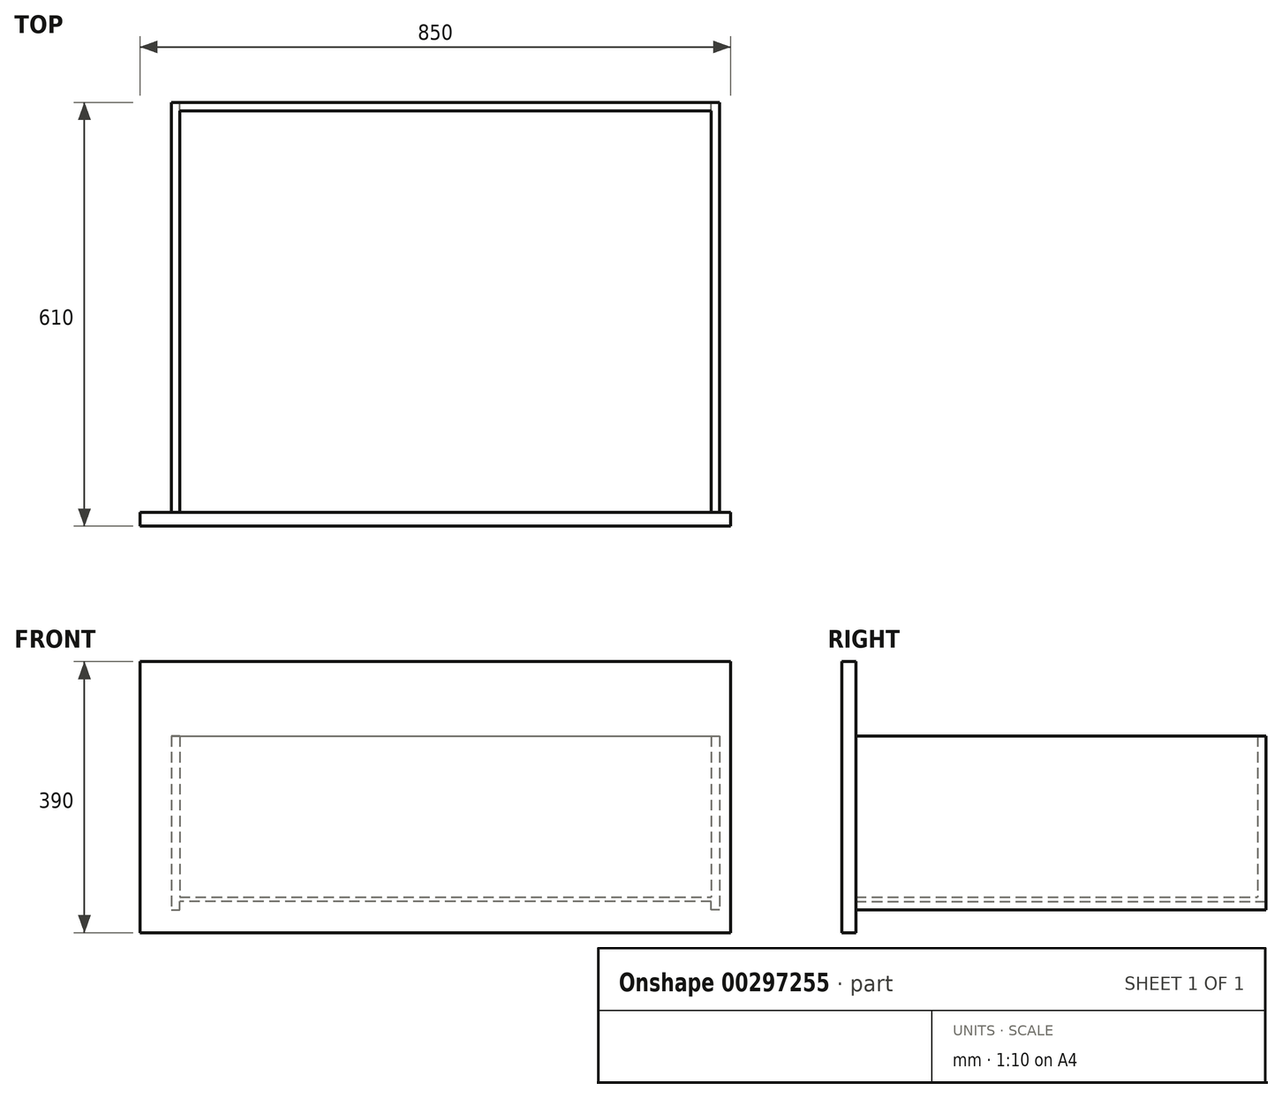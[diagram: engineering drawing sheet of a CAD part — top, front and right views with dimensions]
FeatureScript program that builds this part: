
annotation { "Feature Type Name" : "Feature", "Feature Type Description" : "" }
export const myFeature = defineFeature(function(context is Context, id is Id, definition is map)
    precondition{}
    {
        {
            var Q0;
            Q0=qCreatedBy(makeId("Front.planeOp"),FACE);
            var sketch = newSketch(context, id + "F0", { "sketchPlane" : qUnion([Q0])});
            skLineSegment(sketch, "E0.bottom", {"start": v(382.49, -3) * mm, "end": v(-382.51, -3) * mm});
            skLineSegment(sketch, "E0.top", {"start": v(382.51, 3) * mm, "end": v(-382.49, 3) * mm});
            skPoint(sketch, "E0.middle", {"position": v(0, 0) * mm});
            skLineSegment(sketch, "E1", {"start": v(-382.49, 3) * mm, "end": v(-382.49, 235) * mm});
            skLineSegment(sketch, "E2", {"start": v(-382.49, 235) * mm, "end": v(-394.49, 235) * mm});
            skLineSegment(sketch, "E3", {"start": v(-394.49, 235) * mm, "end": v(-394.49, -15) * mm});
            skLineSegment(sketch, "E4", {"start": v(-394.49, -15) * mm, "end": v(-382.49, -15) * mm});
            skLineSegment(sketch, "E5", {"start": v(-382.49, -15) * mm, "end": v(-382.51, -3) * mm});
            skLineSegment(sketch, "E6", {"start": v(382.51, 3) * mm, "end": v(382.51, 235) * mm});
            skLineSegment(sketch, "E7", {"start": v(382.51, 235) * mm, "end": v(394.51, 235) * mm});
            skLineSegment(sketch, "E8", {"start": v(394.51, 235) * mm, "end": v(394.51, -15) * mm});
            skLineSegment(sketch, "E9", {"start": v(394.51, -15) * mm, "end": v(382.51, -15) * mm});
            skLineSegment(sketch, "E10", {"start": v(382.51, -15) * mm, "end": v(382.49, -3) * mm});
            skSolve(sketch);
        }
        {
            var Q0;
            Q0=qSketchRegion(id+"F0",true);
            extrude(context, id + "F1", {"entities" : qUnion([Q0]), "depth" : 590 * mm});
        }
        {
            var Q0;
            Q0=makeQuery(id+"F1.opExtrude","CAP_FACE",FACE,{"disambiguationData":[OSD([sQuery(id+"F0.wireOp",EDGE,"E0.bottom"),sQuery(id+"F0.wireOp",EDGE,"E0.top"),sQuery(id+"F0.wireOp",EDGE,"E1"),sQuery(id+"F0.wireOp",EDGE,"E2"),sQuery(id+"F0.wireOp",EDGE,"E3"),sQuery(id+"F0.wireOp",EDGE,"E4"),sQuery(id+"F0.wireOp",EDGE,"E5"),sQuery(id+"F0.wireOp",EDGE,"E6"),sQuery(id+"F0.wireOp",EDGE,"E7"),sQuery(id+"F0.wireOp",EDGE,"E8"),sQuery(id+"F0.wireOp",EDGE,"E9"),sQuery(id+"F0.wireOp",EDGE,"E10")])],"isStart":false});
            var sketch = newSketch(context, id + "F2", { "sketchPlane" : qUnion([Q0])});
            skLineSegment(sketch, "E11.bottom", {"start": v(-439.49, 342) * mm, "end": v(410.51, 342) * mm});
            skLineSegment(sketch, "E11.top", {"start": v(-439.49, -48) * mm, "end": v(410.51, -48) * mm});
            skLineSegment(sketch, "E11.left", {"start": v(-439.49, 342) * mm, "end": v(-439.49, -48) * mm});
            skLineSegment(sketch, "E11.right", {"start": v(410.51, 342) * mm, "end": v(410.51, -48) * mm});
            skSolve(sketch);
        }
        {
            var Q0;
            Q0=qSketchRegion(id+"F2",true);
            extrude(context, id + "F3", {"entities" : qUnion([Q0]), "operationType" : NewBodyOperationType.ADD, "depth" : 20 * mm});
        }
        {
            var Q0;
            Q0=makeQuery(id+"F1.opExtrude","SWEPT_FACE",FACE,{"disambiguationData":[OSD([sQuery(id+"F0.wireOp",EDGE,"E6")])]});
            var sketch = newSketch(context, id + "F4", { "sketchPlane" : qUnion([Q0])});
            skLineSegment(sketch, "E12.bottom", {"start": v(0, 235) * mm, "end": v(12, 235) * mm});
            skLineSegment(sketch, "E12.top", {"start": v(0, 3) * mm, "end": v(12, 3) * mm});
            skLineSegment(sketch, "E12.left", {"start": v(0, 235) * mm, "end": v(0, 3) * mm});
            skLineSegment(sketch, "E12.right", {"start": v(12, 235) * mm, "end": v(12, 3) * mm});
            skSolve(sketch);
        }
        {
            var Q0;
            Q0 = qSketchRegion(id + "F4", true);
            extrude(context, id + "F5", {"entities" : qUnion([Q0]), "operationType" : NewBodyOperationType.ADD, "depth" : 765 * mm});
        }
    });
